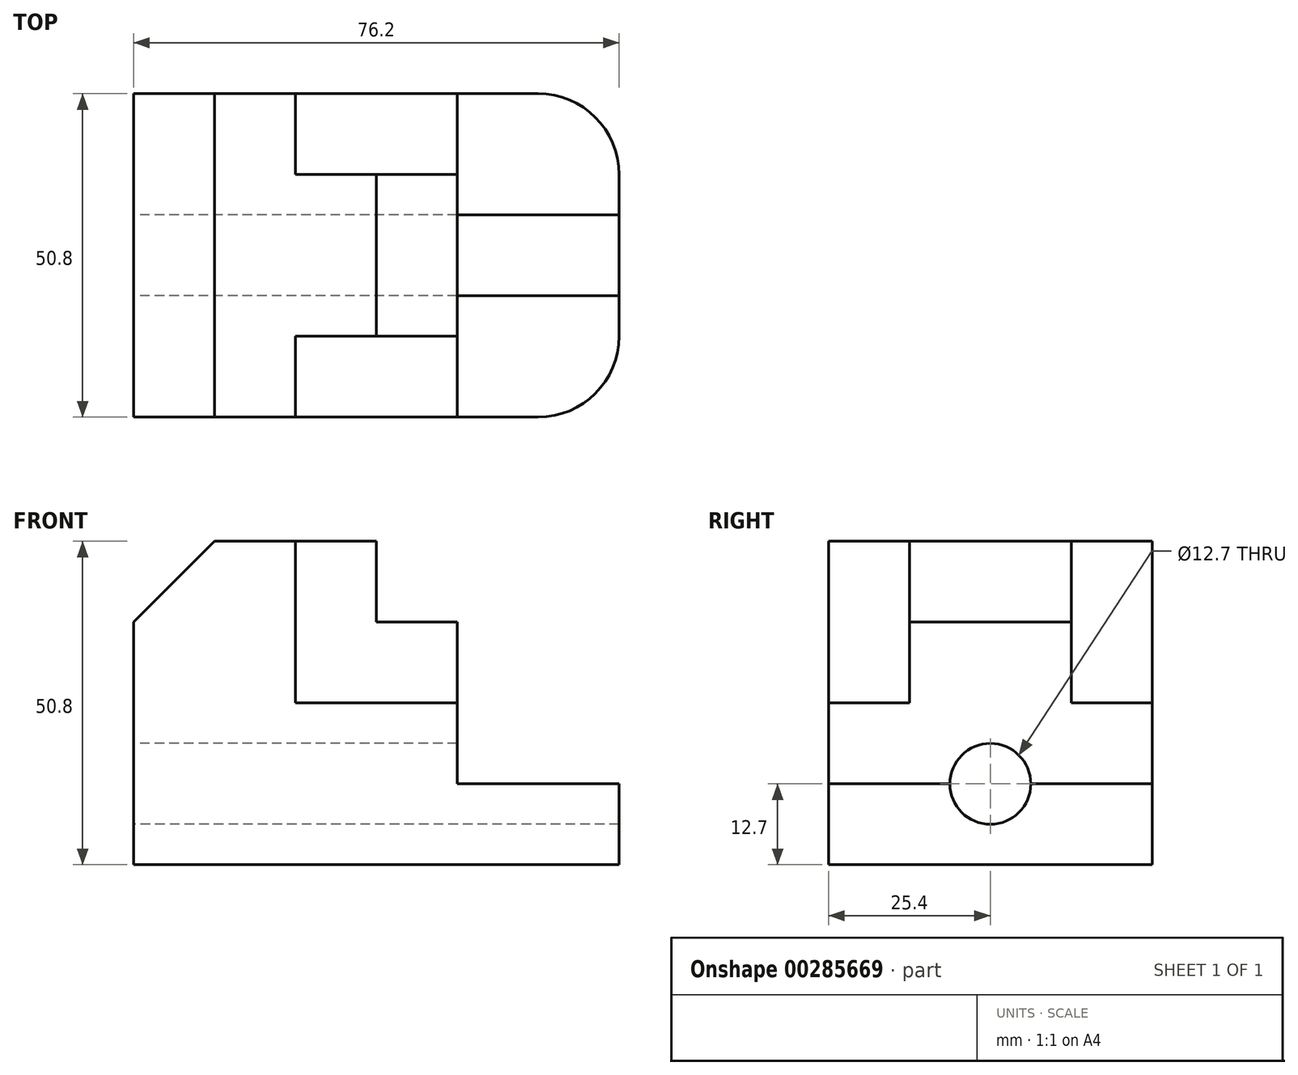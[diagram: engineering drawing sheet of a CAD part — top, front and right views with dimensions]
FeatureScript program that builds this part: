
annotation { "Feature Type Name" : "Feature", "Feature Type Description" : "" }
export const myFeature = defineFeature(function(context is Context, id is Id, definition is map)
    precondition{}
    {
        {
            var Q0;
            Q0=qCreatedBy(makeId("Top.planeOp"),FACE);
            var sketch = newSketch(context, id + "F0", { "sketchPlane" : qUnion([Q0])});
            skLineSegment(sketch, "E0", {"start": v(0, 0) * mm, "end": v(0, 50.8) * mm});
            skLineSegment(sketch, "E1", {"start": v(0, 50.8) * mm, "end": v(63.5, 50.8) * mm});
            skLineSegment(sketch, "E2", {"start": v(0, 0) * mm, "end": v(63.5, 0) * mm});
            skArc(sketch, "E3", {"start": v(76.2, 38.1) * mm, "mid": v(72.48, 47.08) * mm, "end": v(63.5, 50.8) * mm});
            skArc(sketch, "E4", {"start": v(63.5, 0) * mm, "mid": v(72.48, 3.72) * mm, "end": v(76.2, 12.7) * mm});
            skLineSegment(sketch, "E5", {"start": v(76.2, 38.1) * mm, "end": v(76.2, 12.7) * mm});
            skSolve(sketch);
        }
        {
            var Q0;
            Q0 = qSketchRegion(id + "F0", true);
            extrude(context, id + "F1", {"entities" : qUnion([Q0]), "depth" : 12.7 * mm});
        }
        {
            var Q0;
            Q0=makeQuery(id+"F1.opExtrude","CAP_FACE",FACE,{"disambiguationData":[OSD([sQuery(id+"F0.wireOp",EDGE,"E0"),sQuery(id+"F0.wireOp",EDGE,"E1"),sQuery(id+"F0.wireOp",EDGE,"E2"),sQuery(id+"F0.wireOp",EDGE,"E3"),sQuery(id+"F0.wireOp",EDGE,"E4"),sQuery(id+"F0.wireOp",EDGE,"E5")])],"isStart":false});
            var sketch = newSketch(context, id + "F2", { "sketchPlane" : qUnion([Q0])});
            skLineSegment(sketch, "E6", {"start": v(0, 50.8) * mm, "end": v(50.8, 50.8) * mm});
            skLineSegment(sketch, "E7", {"start": v(50.8, 50.8) * mm, "end": v(50.8, 0) * mm});
            skLineSegment(sketch, "E8", {"start": v(50.8, 0) * mm, "end": v(0, 0) * mm});
            skLineSegment(sketch, "E9", {"start": v(0, 0) * mm, "end": v(0, 50.8) * mm});
            skSolve(sketch);
        }
        {
            var Q0;
            Q0 = qSketchRegion(id + "F2", true);
            extrude(context, id + "F3", {"entities" : qUnion([Q0]), "operationType" : NewBodyOperationType.ADD, "depth" : 12.7 * mm});
        }
        {
            var Q0;
            Q0=makeQuery(id+"F3.opExtrude","CAP_FACE",FACE,{"disambiguationData":[OSD([sQuery(id+"F2.wireOp",EDGE,"E6"),sQuery(id+"F2.wireOp",EDGE,"E7"),sQuery(id+"F2.wireOp",EDGE,"E8"),sQuery(id+"F2.wireOp",EDGE,"E9")])],"isStart":false});
            var sketch = newSketch(context, id + "F4", { "sketchPlane" : qUnion([Q0])});
            skLineSegment(sketch, "E10", {"start": v(0, 50.8) * mm, "end": v(25.4, 50.8) * mm});
            skLineSegment(sketch, "E11", {"start": v(25.4, 50.8) * mm, "end": v(25.4, 38.1) * mm});
            skLineSegment(sketch, "E12", {"start": v(25.4, 38.1) * mm, "end": v(50.8, 38.1) * mm});
            skLineSegment(sketch, "E13", {"start": v(50.8, 38.1) * mm, "end": v(50.8, 12.7) * mm});
            skLineSegment(sketch, "E14", {"start": v(50.8, 12.7) * mm, "end": v(25.4, 12.7) * mm});
            skLineSegment(sketch, "E15", {"start": v(25.4, 12.7) * mm, "end": v(25.4, 0) * mm});
            skLineSegment(sketch, "E16", {"start": v(25.4, 0) * mm, "end": v(0, 0) * mm});
            skLineSegment(sketch, "E17", {"start": v(0, 0) * mm, "end": v(0, 50.8) * mm});
            skSolve(sketch);
        }
        {
            var Q0;
            Q0 = qSketchRegion(id + "F4", true);
            extrude(context, id + "F5", {"entities" : qUnion([Q0]), "operationType" : NewBodyOperationType.ADD, "depth" : 12.7 * mm});
        }
        {
            var Q0;
            Q0=makeQuery(id+"F5.opExtrude","CAP_FACE",FACE,{"disambiguationData":[OSD([sQuery(id+"F4.wireOp",EDGE,"E10"),sQuery(id+"F4.wireOp",EDGE,"E11"),sQuery(id+"F4.wireOp",EDGE,"E12"),sQuery(id+"F4.wireOp",EDGE,"E13"),sQuery(id+"F4.wireOp",EDGE,"E14"),sQuery(id+"F4.wireOp",EDGE,"E15"),sQuery(id+"F4.wireOp",EDGE,"E16"),sQuery(id+"F4.wireOp",EDGE,"E17")])],"isStart":false});
            var sketch = newSketch(context, id + "F6", { "sketchPlane" : qUnion([Q0])});
            skLineSegment(sketch, "E18", {"start": v(38.1, 12.7) * mm, "end": v(38.1, 38.1) * mm});
            skLineSegment(sketch, "E19", {"start": v(38.1, 38.1) * mm, "end": v(25.4, 38.1) * mm});
            skLineSegment(sketch, "E20", {"start": v(25.4, 38.1) * mm, "end": v(25.4, 50.8) * mm});
            skLineSegment(sketch, "E21", {"start": v(25.4, 50.8) * mm, "end": v(0, 50.8) * mm});
            skLineSegment(sketch, "E22", {"start": v(0, 50.8) * mm, "end": v(0, 0) * mm});
            skLineSegment(sketch, "E23", {"start": v(0, 0) * mm, "end": v(25.4, 0) * mm});
            skLineSegment(sketch, "E24", {"start": v(25.4, 0) * mm, "end": v(25.4, 12.7) * mm});
            skLineSegment(sketch, "E25", {"start": v(25.4, 12.7) * mm, "end": v(38.1, 12.7) * mm});
            skSolve(sketch);
        }
        {
            var Q0;
            Q0 = qSketchRegion(id + "F6", true);
            extrude(context, id + "F7", {"entities" : qUnion([Q0]), "operationType" : NewBodyOperationType.ADD, "depth" : 12.7 * mm});
        }
        {
            var Q0;
            Q0=makeQuery(id+"F7.boolean.opBoolean","MERGE",FACE,{"derivedFrom":[makeQuery(id+"F5.boolean.opBoolean","MERGE",FACE,{"derivedFrom":[makeQuery(id+"F3.boolean.opBoolean","MERGE",FACE,{"derivedFrom":[makeQuery(id+"F1.opExtrude","SWEPT_FACE",FACE,{"disambiguationData":[OSD([sQuery(id+"F0.wireOp",EDGE,"E2")])]}),makeQuery(id+"F3.opExtrude","SWEPT_FACE",FACE,{"disambiguationData":[OSD([sQuery(id+"F2.wireOp",EDGE,"E8")])]})]}),makeQuery(id+"F5.opExtrude","SWEPT_FACE",FACE,{"disambiguationData":[OSD([sQuery(id+"F4.wireOp",EDGE,"E16")])]})]}),makeQuery(id+"F7.opExtrude","SWEPT_FACE",FACE,{"disambiguationData":[OSD([sQuery(id+"F6.wireOp",EDGE,"E23")])]})]});
            var sketch = newSketch(context, id + "F8", { "sketchPlane" : qUnion([Q0])});
            skLineSegment(sketch, "E26", {"start": v(12.7, 50.8) * mm, "end": v(0, 38.1) * mm});
            skLineSegment(sketch, "E27", {"start": v(0, 38.1) * mm, "end": v(0, 50.8) * mm});
            skLineSegment(sketch, "E28", {"start": v(0, 50.8) * mm, "end": v(12.7, 50.8) * mm});
            skSolve(sketch);
        }
        {
            var Q0;
            Q0 = qSketchRegion(id + "F8", true);
            extrude(context, id + "F9", {"entities" : qUnion([Q0]), "operationType" : NewBodyOperationType.REMOVE, "oppositeDirection" : true, "depth" : 50.8 * mm});
        }
        {
            var Q0;
            Q0=makeQuery(id+"F7.boolean.opBoolean","MERGE",FACE,{"derivedFrom":[makeQuery(id+"F5.boolean.opBoolean","MERGE",FACE,{"derivedFrom":[makeQuery(id+"F3.boolean.opBoolean","MERGE",FACE,{"derivedFrom":[makeQuery(id+"F1.opExtrude","SWEPT_FACE",FACE,{"disambiguationData":[OSD([sQuery(id+"F0.wireOp",EDGE,"E0")])]}),makeQuery(id+"F3.opExtrude","SWEPT_FACE",FACE,{"disambiguationData":[OSD([sQuery(id+"F2.wireOp",EDGE,"E9")])]})]}),makeQuery(id+"F5.opExtrude","SWEPT_FACE",FACE,{"disambiguationData":[OSD([sQuery(id+"F4.wireOp",EDGE,"E17")])]})]}),makeQuery(id+"F7.opExtrude","SWEPT_FACE",FACE,{"disambiguationData":[OSD([sQuery(id+"F6.wireOp",EDGE,"E22")])]})]});
            var sketch = newSketch(context, id + "F10", { "sketchPlane" : qUnion([Q0])});
            skCircle(sketch, "E29", {"center": v(-25.4, 12.7) * mm, "radius": 6.35 * mm});
            skSolve(sketch);
        }
        {
            var Q0;
            Q0 = qSketchRegion(id + "F10", true);
            extrude(context, id + "F11", {"entities" : qUnion([Q0]), "operationType" : NewBodyOperationType.REMOVE, "oppositeDirection" : true, "depth" : 76.2 * mm});
        }
    });
